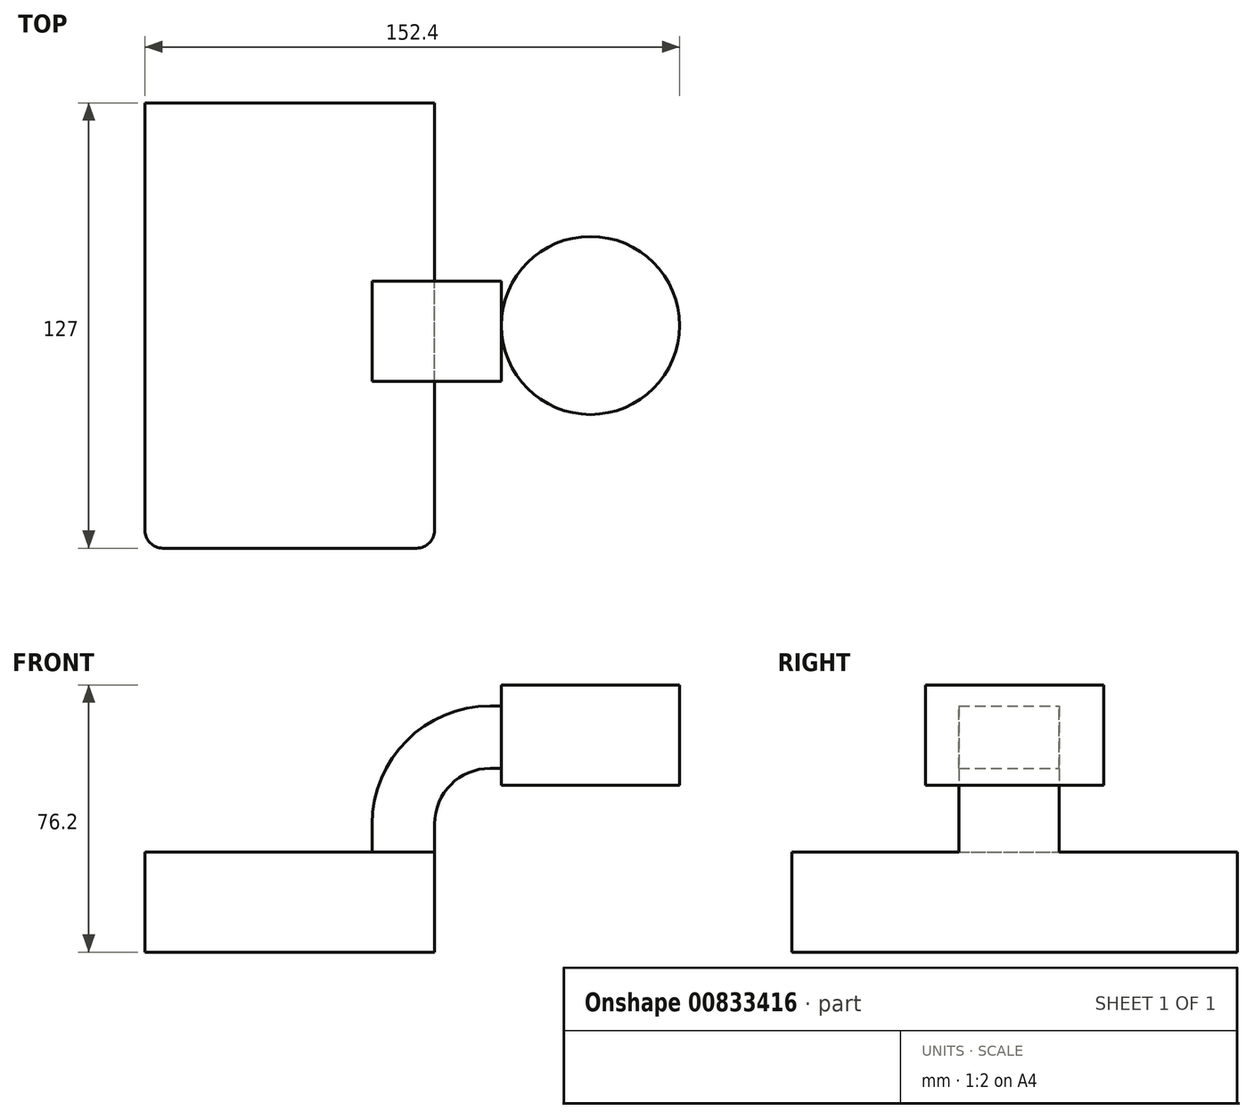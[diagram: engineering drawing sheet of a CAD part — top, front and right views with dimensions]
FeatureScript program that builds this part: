
annotation { "Feature Type Name" : "Feature", "Feature Type Description" : "" }
export const myFeature = defineFeature(function(context is Context, id is Id, definition is map)
    precondition{}
    {
        {
            var Q0;
            Q0=qCreatedBy(makeId("Front.planeOp"),FACE);
            var sketch = newSketch(context, id + "F0", { "sketchPlane" : qUnion([Q0])});
            skLineSegment(sketch, "E0.bottom", {"start": v(41.28, -14.29) * mm, "end": v(-41.28, -14.29) * mm});
            skLineSegment(sketch, "E0.top", {"start": v(41.28, 14.29) * mm, "end": v(-41.28, 14.29) * mm});
            skLineSegment(sketch, "E0.left", {"start": v(41.28, -14.29) * mm, "end": v(41.28, 14.29) * mm});
            skLineSegment(sketch, "E0.right", {"start": v(-41.28, -14.29) * mm, "end": v(-41.28, 14.29) * mm});
            skPoint(sketch, "E0.middle", {"position": v(0, 0) * mm});
            skLineSegment(sketch, "E1.bottom", {"start": v(111.13, 33.34) * mm, "end": v(60.33, 33.34) * mm});
            skLineSegment(sketch, "E1.top", {"start": v(111.13, 61.91) * mm, "end": v(60.33, 61.91) * mm});
            skLineSegment(sketch, "E1.left", {"start": v(111.13, 33.34) * mm, "end": v(111.13, 61.91) * mm});
            skLineSegment(sketch, "E1.right", {"start": v(60.33, 33.34) * mm, "end": v(60.33, 61.91) * mm});
            skPoint(sketch, "E1.middle", {"position": v(85.73, 47.62) * mm});
            skLineSegment(sketch, "E2", {"start": v(41.28, 14.29) * mm, "end": v(41.28, 22.24) * mm});
            skArc(sketch, "E3", {"start": v(41.28, 22.24) * mm, "mid": v(45.92, 33.46) * mm, "end": v(57.15, 38.11) * mm});
            skLineSegment(sketch, "E4", {"start": v(57.15, 38.11) * mm, "end": v(85.73, 38.11) * mm});
            skLineSegment(sketch, "E5.0", {"start": v(57.15, 55.9) * mm, "end": v(85.73, 55.9) * mm});
            skArc(sketch, "E5.1", {"start": v(23.5, 22.24) * mm, "mid": v(33.35, 46.04) * mm, "end": v(57.15, 55.9) * mm});
            skLineSegment(sketch, "E5.2", {"start": v(23.5, 14.29) * mm, "end": v(23.5, 22.24) * mm});
            skLineSegment(sketch, "E6", {"start": v(85.73, 61.91) * mm, "end": v(85.73, 33.34) * mm});
            skFitSpline(sketch, "E7", {"points": [v(-41.28, 14.29) * mm, v(57.15, 55.9) * mm], "startDerivative": vector(-8.3, 137.28) * mm, "endDerivative": vector(184.48, -1.01) * mm});
            skSolve(sketch);
        }
        {
            var Q0;
            Q0=makeQuery(id+"F0.imprint","IMPRINT",FACE,{"disambiguationData":[TD([[makeQuery(id+"F0.imprint","IMPRINT",EDGE,{"derivedFrom":sQuery(id+"F0.wireOp",EDGE,"E0.bottom")}),-1.0]])]});
            extrude(context, id + "F1", {"entities" : qUnion([Q0]), "endBound" : BoundingType.SYMMETRIC, "depth" : 127 * mm, "offsetDistance" : 25.4 * mm});
        }
        {
            var Q0;
            {var subQ1=sQuery(id+"F0.wireOp",EDGE,"E2");Q0=makeQuery(id+"F0.imprint","IMPRINT",FACE,{"disambiguationData":[TD([[makeQuery(id+"F0.imprint","IMPRINT",EDGE,{"derivedFrom":subQ1}),1.0]])]});}
            extrude(context, id + "F2", {"entities" : qUnion([Q0]), "operationType" : NewBodyOperationType.ADD, "endBound" : BoundingType.SYMMETRIC, "depth" : 25.4 * mm, "offsetDistance" : 25.4 * mm});
        }
        {
            var Q0;
            Q0=makeQuery(id+"F0.imprint","IMPRINT",FACE,{"disambiguationData":[TD([[makeQuery(id+"F0.imprint","IMPRINT",EDGE,{"derivedFrom":sQuery(id+"F0.wireOp",EDGE,"E5.1")}),1.0]])]});
            extrude(context, id + "F3", {"entities" : qUnion([Q0]), "operationType" : NewBodyOperationType.ADD, "depth" : 15.88 * mm, "offsetDistance" : 25.4 * mm});
        }
        {
            var Q0;
            {var subQ4=sQuery(id+"F0.wireOp",EDGE,"E1.left");Q0=makeQuery(id+"F0.imprint","IMPRINT",FACE,{"disambiguationData":[TD([[makeQuery(id+"F0.imprint","IMPRINT",EDGE,{"derivedFrom":subQ4}),1.0]])]});}
            var Q1;
            Q1=sQuery(id+"F0.wireOp",EDGE,"E6");
            revolve(context, id + "F4", {"operationType" : NewBodyOperationType.ADD, "surfaceOperationType" : NewSurfaceOperationType.NEW, "entities" : qUnion([Q0]), "axis" : qUnion([Q1]), "revolveType" : RevolveType.FULL});
        }
        {
            var Q0;
            Q0=makeQuery(id+"F1.opExtrude","CAP_EDGE",EDGE,{"disambiguationData":[OSD([sQuery(id+"F0.wireOp",EDGE,"E0.right")])],"isStart":false});
            var Q1;
            Q1=makeQuery(id+"F1.opExtrude","CAP_EDGE",EDGE,{"disambiguationData":[OSD([sQuery(id+"F0.wireOp",EDGE,"E0.left")])],"isStart":false});
            fillet(context, id + "F5", {"entities" : qUnion([Q0, Q1]), "radius" : 5.08 * mm, "tangentPropagation" : true, "allowEdgeOverflow" : false});
        }
    });
